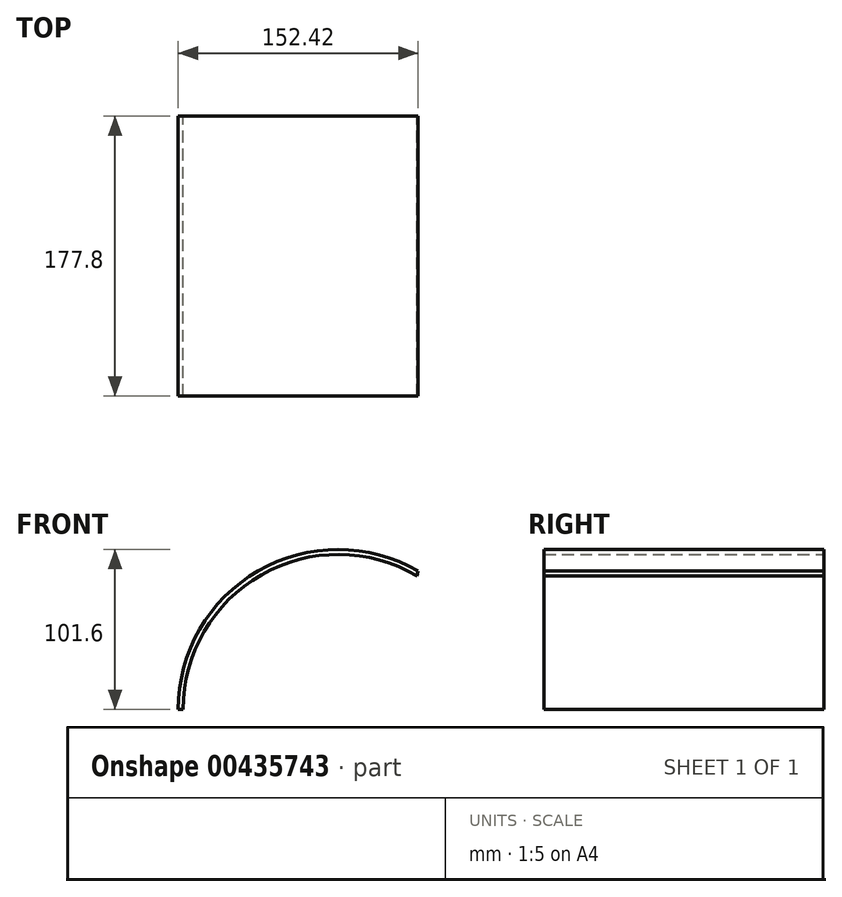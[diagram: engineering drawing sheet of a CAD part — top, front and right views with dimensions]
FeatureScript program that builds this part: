
annotation { "Feature Type Name" : "Feature", "Feature Type Description" : "" }
export const myFeature = defineFeature(function(context is Context, id is Id, definition is map)
    precondition{}
    {
        {
            var Q0;
            Q0=qCreatedBy(makeId("Front.planeOp"),FACE);
            var sketch = newSketch(context, id + "F0", { "sketchPlane" : qUnion([Q0])});
            skArc(sketch, "E0", {"start": v(50.82, 87.98) * mm, "mid": v(-50.8, 88) * mm, "end": v(-101.6, 0) * mm});
            skArc(sketch, "E1", {"start": v(50, 84.8) * mm, "mid": v(-48.77, 85.5) * mm, "end": v(-98.43, 0.12) * mm});
            skLineSegment(sketch, "E2", {"start": v(50.82, 87.98) * mm, "end": v(50, 84.8) * mm});
            skLineSegment(sketch, "E3", {"start": v(-98.43, 0.12) * mm, "end": v(-101.6, 0) * mm});
            skLineSegment(sketch, "E4", {"start": v(-101.6, 0) * mm, "end": v(0, 0) * mm, "construction": true});
            skLineSegment(sketch, "E5", {"start": v(50.82, 87.98) * mm, "end": v(0.02, 0) * mm, "construction": true});
            skSolve(sketch);
        }
        {
            var Q0;
            Q0 = qSketchRegion(id + "F0", true);
            extrude(context, id + "F1", {"entities" : qUnion([Q0]), "depth" : 177.8 * mm});
        }
    });
